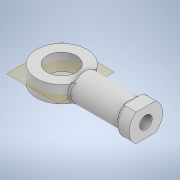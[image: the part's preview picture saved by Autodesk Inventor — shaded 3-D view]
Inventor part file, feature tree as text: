
AUTODESK INVENTOR PART (.ipt)
format: ipt  version: 2020 (Build 240168000, 168)  size: 276,992 bytes
history: native  units: mm
features: sketch x6, extrude x5, fillet x5, projected_geometry x5, thicken_offset x2, plane x1, revolve x1
ambient origin geometry x8: Origin, YZ Plane, XZ Plane, XY Plane, X Axis, Y Axis, Z Axis, Center Point
bodies: Solid1 (feature_tree)
feature tree (25):
  extrude  "Extrusion1"  Depth=4.0mm TaperAngle=0.0deg
  extrude  "Extrusion2"  Depth=20.0mm TaperAngle=0.0deg
  thicken_offset  "Thicken1"
  thicken_offset  "Thicken2"
  fillet  "Fillet1"  Radius=5.5mm
  fillet  "Fillet2"  Radius=5.5mm
  fillet  "Fillet3"  Radius=5.5mm
  extrude  "Extrusion3"  Depth=0.5mm
  plane  "Work Plane1"
  revolve  "Revolution1"  [1 undecoded]
  extrude  "Extrusion4"  Depth=10.0mm TaperAngle=0.0deg
  extrude  "Extrusion5"  Depth=0.5mm
  fillet  "Fillet4"  [1 undecoded]
  fillet  "Fillet5"  Radius=8.0mm
  sketch  "Sketch1"  dims[d0=12.0mm d1=4.0mm d2=0.0mm]
  sketch  "Sketch2"  dims[d3=6.5mm d4=20.0mm d5=0.0mm d6=5.5mm d7=5.5mm d8=5.5mm]
  projected_geometry  "Projected Loop1"
  sketch  "Sketch3"  dims[d9=5.5mm d10=0.5mm]
  projected_geometry  "Projected Loop2"
  sketch  "Sketch4"  dims[d11=0.5mm d12=0.5mm]
  projected_geometry  "Projected Loop3"
  sketch  "Sketch5"  dims[d13=3.0mm d14=10.0mm d15=0.0mm]
  projected_geometry  "Projected Loop4"
  sketch  "Sketch6"  dims[d16=-2.0mm d17=8.0mm d18=90.0deg d19=8.0mm d20=3.0mm d21=0.0mm d22=6.5mm d23=10.0mm d24=3.0mm d25=0.0mm d26=0.5mm d27=0.5mm]
  projected_geometry  "Projected Loop5"
note: 2 required parameter values undecoded (feature->parameter linkage not recoverable at this tier; creation-order binding heuristic only, values carry confidence <= 0.55)